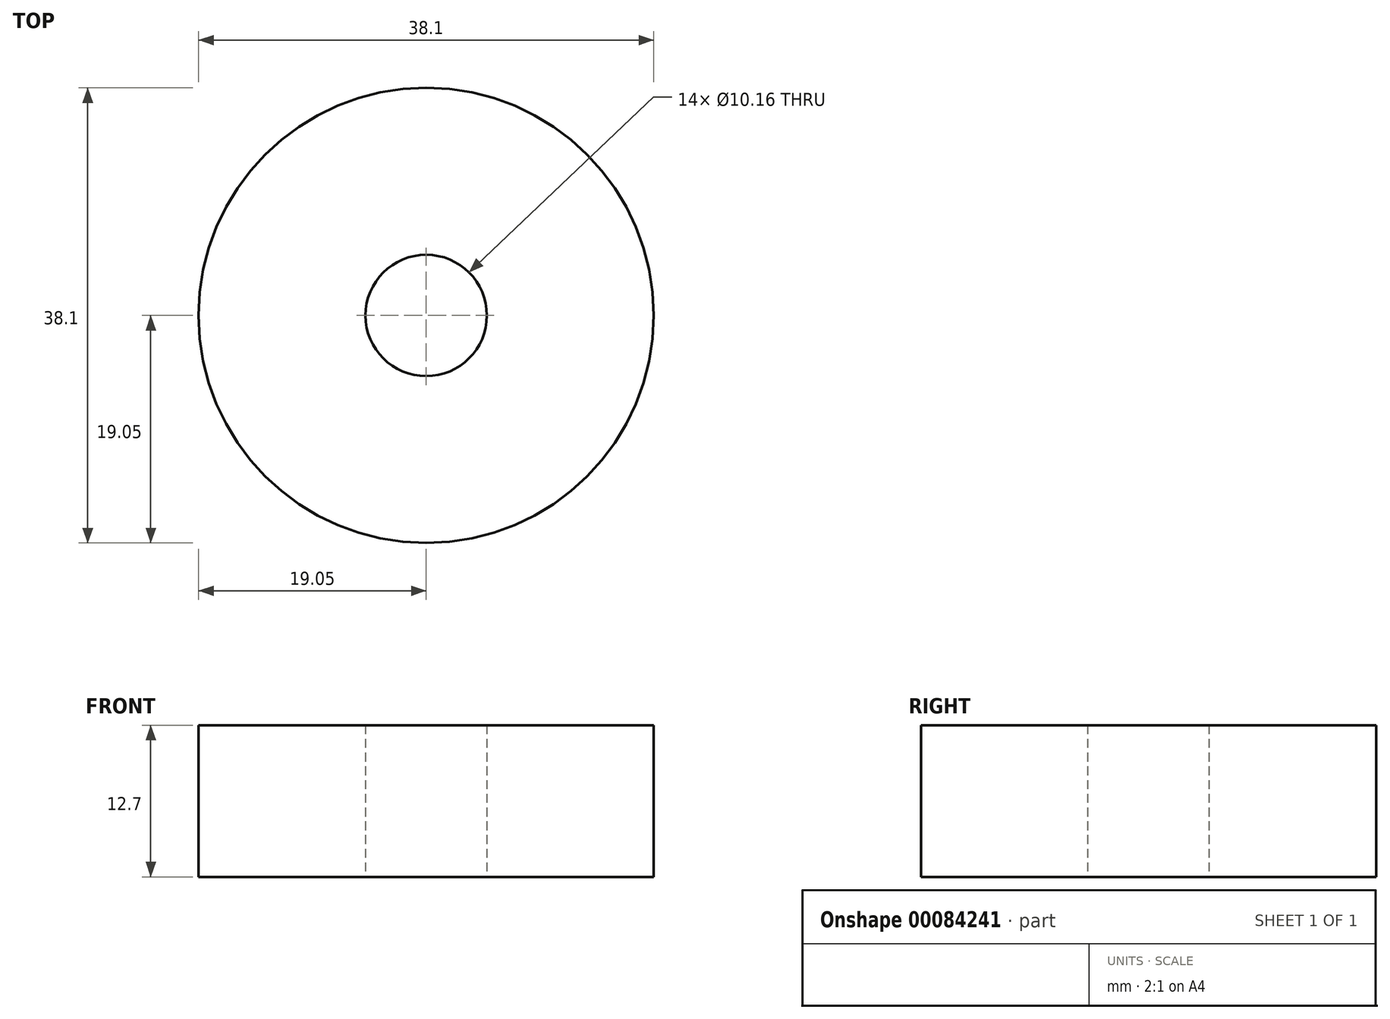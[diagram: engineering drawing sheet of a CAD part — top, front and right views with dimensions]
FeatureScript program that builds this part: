
annotation { "Feature Type Name" : "Feature", "Feature Type Description" : "" }
export const myFeature = defineFeature(function(context is Context, id is Id, definition is map)
    precondition{}
    {
        {
            var Q0;
            Q0=qCreatedBy(makeId("Top.planeOp"),FACE);
            var sketch = newSketch(context, id + "F0", { "sketchPlane" : qUnion([Q0])});
            skCircle(sketch, "E0", {"center": v(0, 0) * mm, "radius": 19.05 * mm});
            skCircle(sketch, "E1", {"center": v(0, 0) * mm, "radius": 5.08 * mm});
            skPoint(sketch, "E2", {"position": v(-19.05, 0) * mm});
            skSolve(sketch);
        }
        {
            var Q0;
            Q0=makeQuery(id+"F0.imprint","IMPRINT",FACE,{"disambiguationData":[TD([[makeQuery(id+"F0.imprint","IMPRINT",EDGE,{"derivedFrom":sQuery(id+"F0.wireOp",EDGE,"E0")}),1.0]])]});
            extrude(context, id + "F1", {"entities" : qUnion([Q0]), "endBound" : BoundingType.SYMMETRIC, "depth" : 12.7 * mm});
        }
    });
